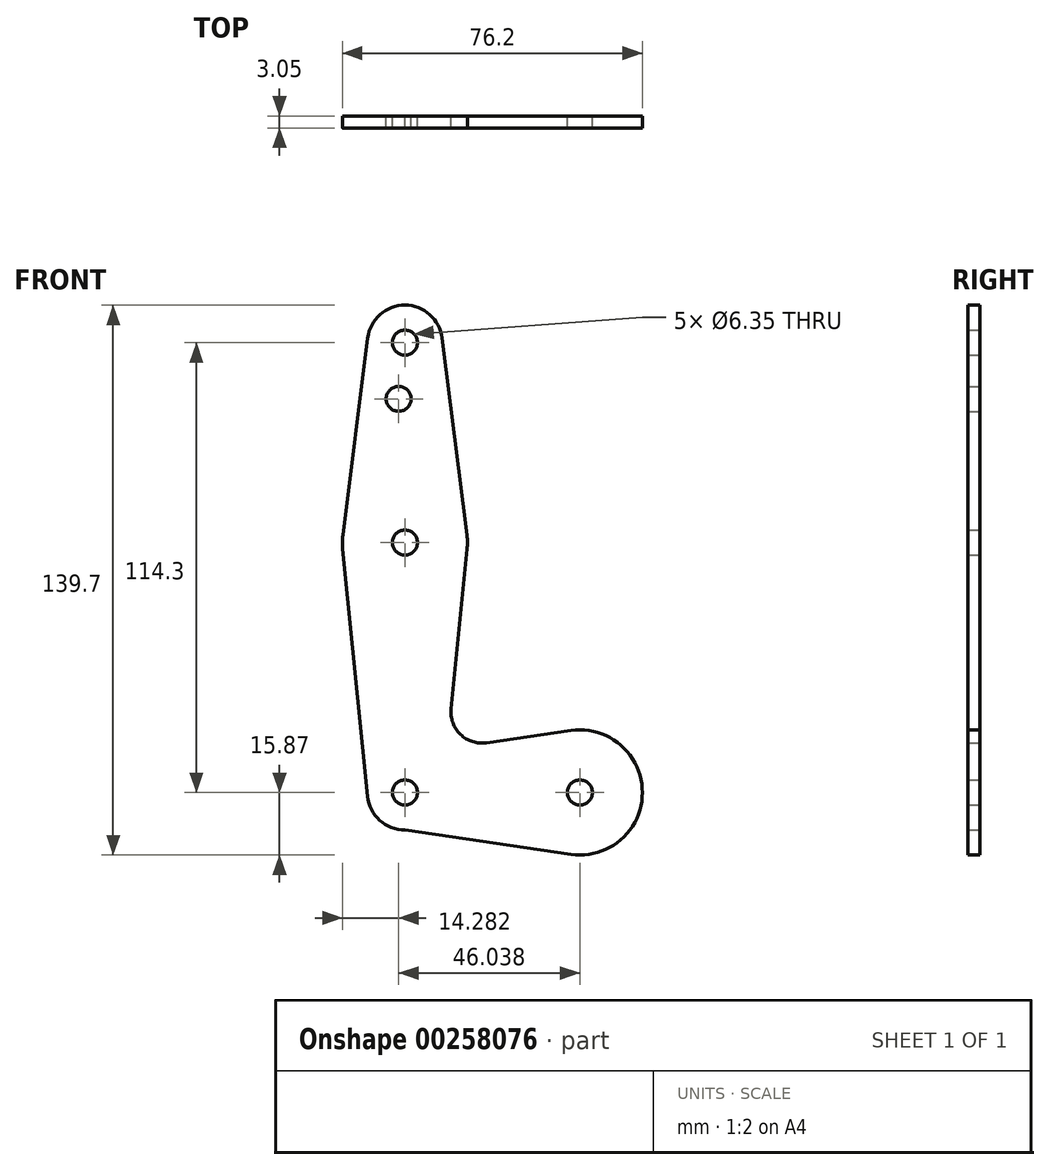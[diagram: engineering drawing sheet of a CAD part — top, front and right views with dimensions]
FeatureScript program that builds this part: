
annotation { "Feature Type Name" : "Feature", "Feature Type Description" : "" }
export const myFeature = defineFeature(function(context is Context, id is Id, definition is map)
    precondition{}
    {
        {
            var Q0;
            Q0=qCreatedBy(makeId("Front.planeOp"),FACE);
            var sketch = newSketch(context, id + "F0", { "sketchPlane" : qUnion([Q0])});
            skLineSegment(sketch, "E0", {"start": v(0, 0) * mm, "end": v(0, 114.3) * mm, "construction": true});
            skLineSegment(sketch, "E1", {"start": v(0, 0) * mm, "end": v(44.45, 0) * mm, "construction": true});
            skCircle(sketch, "E2", {"center": v(0, 114.3) * mm, "radius": 9.53 * mm});
            skCircle(sketch, "E3", {"center": v(0, 63.5) * mm, "radius": 15.88 * mm});
            skCircle(sketch, "E4", {"center": v(0, 0) * mm, "radius": 9.53 * mm});
            skCircle(sketch, "E5", {"center": v(44.45, 0) * mm, "radius": 15.88 * mm});
            skLineSegment(sketch, "E6", {"start": v(-9.45, 115.5) * mm, "end": v(-15.98, 63.7) * mm});
            skLineSegment(sketch, "E7", {"start": v(9.45, 115.5) * mm, "end": v(15.95, 63.86) * mm});
            skLineSegment(sketch, "E8", {"start": v(-9.48, -0.95) * mm, "end": v(-15.8, 61.91) * mm});
            skLineSegment(sketch, "E9", {"start": v(15.95, 63.5) * mm, "end": v(11.71, 21.28) * mm});
            skLineSegment(sketch, "E10", {"start": v(20.76, 12.62) * mm, "end": v(42.18, 15.71) * mm});
            skLineSegment(sketch, "E11", {"start": v(0, -9.52) * mm, "end": v(42.15, -15.7) * mm});
            skCircle(sketch, "E12", {"center": v(0, 114.3) * mm, "radius": 3.18 * mm});
            skCircle(sketch, "E13", {"center": v(0, 63.5) * mm, "radius": 3.18 * mm});
            skCircle(sketch, "E14", {"center": v(0, 0) * mm, "radius": 3.18 * mm});
            skCircle(sketch, "E15", {"center": v(44.45, 0) * mm, "radius": 3.17 * mm});
            skCircle(sketch, "E16", {"center": v(-1.59, 100.03) * mm, "radius": 3.18 * mm});
            skArc(sketch, "E17.filletArc", {"start": v(11.71, 21.28) * mm, "mid": v(14.12, 14.75) * mm, "end": v(20.76, 12.62) * mm});
            skSolve(sketch);
        }
        {
            var Q0;
            Q0 = qSketchRegion(id + "F0", true);
            extrude(context, id + "F1", {"entities" : qUnion([Q0]), "depth" : 3.05 * mm});
        }
    });
